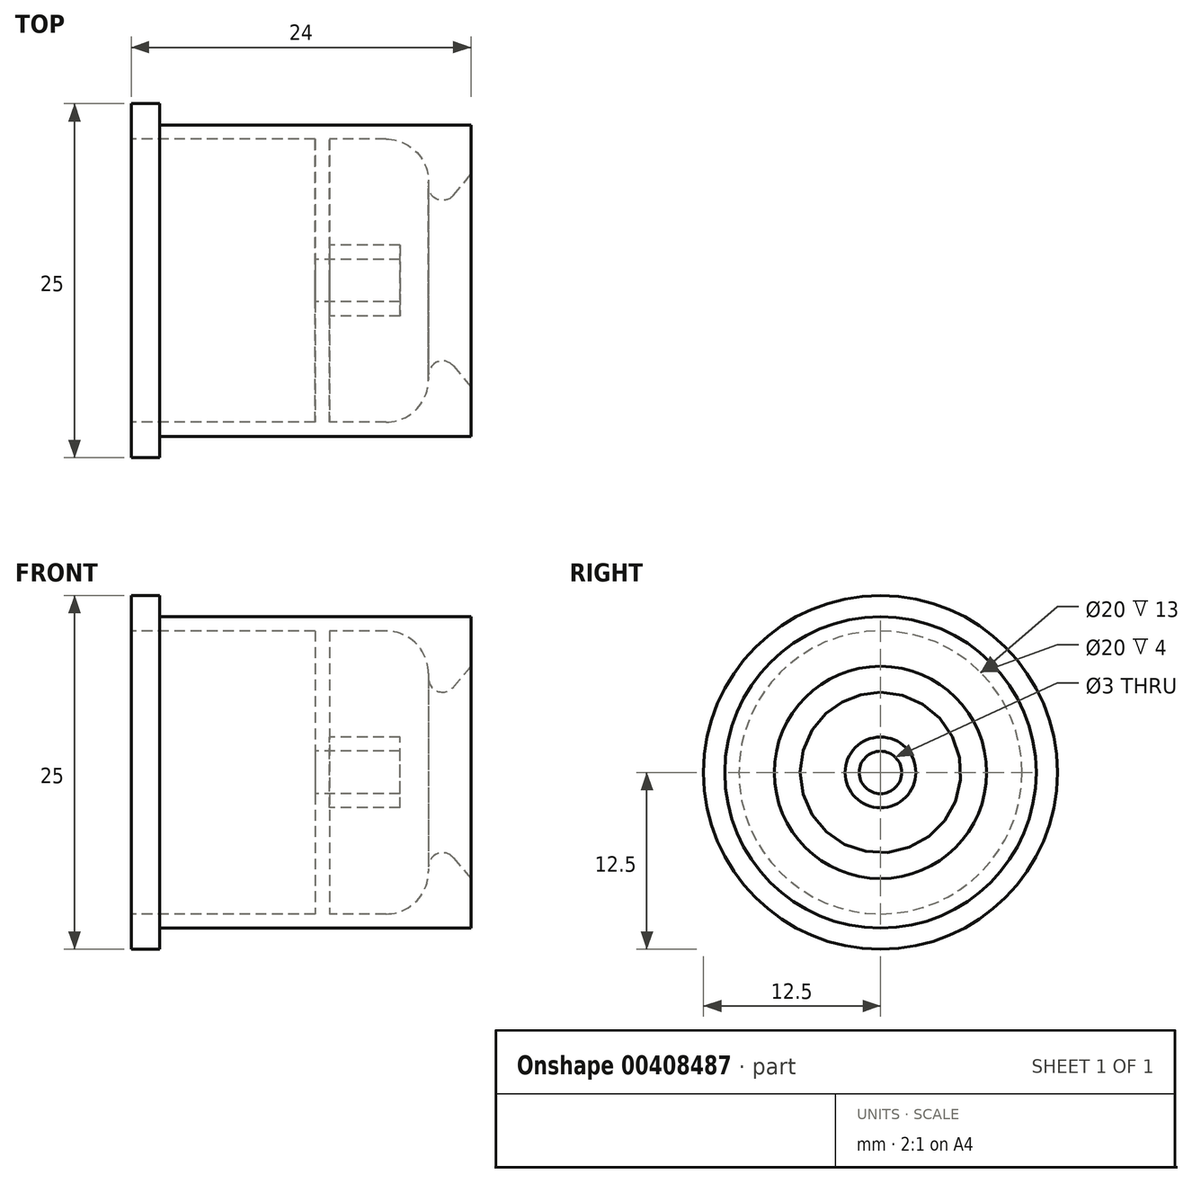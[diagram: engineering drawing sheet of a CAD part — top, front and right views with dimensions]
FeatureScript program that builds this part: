
annotation { "Feature Type Name" : "Feature", "Feature Type Description" : "" }
export const myFeature = defineFeature(function(context is Context, id is Id, definition is map)
    precondition{}
    {
        {
            var Q0;
            Q0=qCreatedBy(makeId("Front.planeOp"),FACE);
            var sketch = newSketch(context, id + "F0", { "sketchPlane" : qUnion([Q0])});
            skLineSegment(sketch, "E0", {"start": v(-26.94, 0) * mm, "end": v(26.94, 0) * mm, "construction": true});
            skLineSegment(sketch, "E1", {"start": v(-24, 10) * mm, "end": v(-6, 10) * mm});
            skLineSegment(sketch, "E2", {"start": v(-3, 7) * mm, "end": v(-3, 6.67) * mm});
            skLineSegment(sketch, "E3", {"start": v(-1.23, 6.03) * mm, "end": v(0, 7.5) * mm});
            skLineSegment(sketch, "E4", {"start": v(0, 7.5) * mm, "end": v(0, 11) * mm});
            skLineSegment(sketch, "E5", {"start": v(-22, 11) * mm, "end": v(-22, 12.5) * mm});
            skLineSegment(sketch, "E6", {"start": v(-22, 11) * mm, "end": v(0, 11) * mm});
            skLineSegment(sketch, "E7", {"start": v(-22, 12.5) * mm, "end": v(-24, 12.5) * mm});
            skLineSegment(sketch, "E8", {"start": v(-24, 12.5) * mm, "end": v(-24, 10) * mm});
            skPoint(sketch, "E9.visualSharp", {"position": v(-3, 10) * mm});
            skArc(sketch, "E9.filletArc", {"start": v(-3, 7) * mm, "mid": v(-3.88, 9.12) * mm, "end": v(-6, 10) * mm});
            skPoint(sketch, "E10.visualSharp", {"position": v(-3, 3.92) * mm});
            skArc(sketch, "E10.filletArc", {"start": v(-3, 6.67) * mm, "mid": v(-2.34, 5.73) * mm, "end": v(-1.23, 6.03) * mm});
            skSolve(sketch);
        }
        {
            var Q0;
            Q0=makeQuery(id+"F0.imprint","IMPRINT",FACE,{"disambiguationData":[TD([[makeQuery(id+"F0.imprint","IMPRINT",EDGE,{"derivedFrom":sQuery(id+"F0.wireOp",EDGE,"E1")}),1.0]])]});
            var Q1;
            Q1=sQuery(id+"F0.wireOp",EDGE,"E0");
            revolve(context, id + "F1", {"entities" : qUnion([Q0]), "axis" : qUnion([Q1]), "revolveType" : RevolveType.FULL});
        }
        {
            var Q0;
            Q0=makeQuery(id+"F1.opRevolve","SWEPT_FACE",FACE,{"disambiguationData":[OSD([sQuery(id+"F0.wireOp",EDGE,"E4")])]});
            cPlane(context, id + "F2", {"entities" : qUnion([Q0]), "cplaneType" : CPlaneType.OFFSET, "offset" : 11 * mm, "oppositeDirection" : true, "width" : 150 * mm, "height" : 150 * mm});
        }
        {
            var Q0;
            Q0=qCreatedBy(id+"F2.planeOp",FACE);
            var sketch = newSketch(context, id + "F3", { "sketchPlane" : qUnion([Q0])});
            skCircle(sketch, "E11", {"center": v(0, 0) * mm, "radius": 2.5 * mm});
            skSolve(sketch);
        }
        {
            var Q0;
            Q0=makeQuery(id+"F3.imprint","IMPRINT",FACE,{"disambiguationData":[TD([[makeQuery(id+"F3.imprint","IMPRINT",EDGE,{"derivedFrom":sQuery(id+"F3.wireOp",EDGE,"E11")}),1.0]])]});
            extrude(context, id + "F4", {"entities" : qUnion([Q0]), "depth" : 6 * mm});
        }
        {
            var Q0;
            Q0=makeQuery(id+"F4.opExtrude","CAP_FACE",FACE,{"disambiguationData":[OSD([sQuery(id+"F3.wireOp",EDGE,"E11")])],"isStart":true});
            var sketch = newSketch(context, id + "F5", { "sketchPlane" : qUnion([Q0])});
            skCircle(sketch, "E12.0", {"center": v(0, 0) * mm, "radius": 10 * mm});
            skLineSegment(sketch, "E13", {"start": v(0, 0) * mm, "end": v(0, 10) * mm, "construction": true});
            skLineSegment(sketch, "E14.0", {"start": v(0.75, 0) * mm, "end": v(0.75, 9.97) * mm});
            skLineSegment(sketch, "E15.0", {"start": v(-0.75, 0) * mm, "end": v(-0.75, 9.97) * mm});
            skLineSegment(sketch, "E16", {"start": v(-0.75, 0) * mm, "end": v(0.75, 0) * mm});
            skArc(sketch, "E17", {"start": v(-0.75, 9.97) * mm, "mid": v(0, 10) * mm, "end": v(0.75, 9.97) * mm});
            skSolve(sketch);
        }
        {
            var Q0;
            {var subQ0=sQuery(id+"F5.wireOp",EDGE,"E14.0");var subQ1=sQuery(id+"F5.wireOp",EDGE,"E12.0");var subQ2=makeQuery(id+"F5.imprint","INTERSECT",VERTEX,{"derivedFrom":[subQ1,subQ0]});Q0=makeQuery(id+"F5.imprint","IMPRINT",FACE,{"disambiguationData":[TD([[makeQuery(id+"F5.imprint","IMPRINT",EDGE,{"disambiguationData":[TD([[subQ2,-1.0]])],"derivedFrom":subQ1}),1.0]])]});}
            extrude(context, id + "F6", {"entities" : qUnion([Q0]), "operationType" : NewBodyOperationType.ADD, "oppositeDirection" : true, "depth" : 1 * mm});
        }
        {
            var Q0;
            Q0=makeQuery(id+"F1.opRevolve","SWEPT_BODY",BODY,{"disambiguationData":[OSD([sQuery(id+"F0.wireOp",EDGE,"E1"),sQuery(id+"F0.wireOp",EDGE,"E2"),sQuery(id+"F0.wireOp",EDGE,"E3"),sQuery(id+"F0.wireOp",EDGE,"E4"),sQuery(id+"F0.wireOp",EDGE,"E5"),sQuery(id+"F0.wireOp",EDGE,"E6"),sQuery(id+"F0.wireOp",EDGE,"E7"),sQuery(id+"F0.wireOp",EDGE,"E8"),sQuery(id+"F0.wireOp",EDGE,"E9.filletArc"),sQuery(id+"F0.wireOp",EDGE,"E10.filletArc")])]});
            var Q1;
            Q1=makeQuery(id+"F4.opExtrude","CAP_EDGE",EDGE,{"disambiguationData":[OSD([sQuery(id+"F3.wireOp",EDGE,"E11")])],"isStart":true});
            circularPattern(context, id + "F7", {"entities" : qUnion([Q0]), "axis" : qUnion([Q1]), "angle" : 360 * degree, "instanceCount" : 3, "equalSpace" : true});
        }
        {
            var Q0;
            Q0=makeQuery(id+"F1.opRevolve","SWEPT_BODY",BODY,{"disambiguationData":[OSD([sQuery(id+"F0.wireOp",EDGE,"E1"),sQuery(id+"F0.wireOp",EDGE,"E2"),sQuery(id+"F0.wireOp",EDGE,"E3"),sQuery(id+"F0.wireOp",EDGE,"E4"),sQuery(id+"F0.wireOp",EDGE,"E5"),sQuery(id+"F0.wireOp",EDGE,"E6"),sQuery(id+"F0.wireOp",EDGE,"E7"),sQuery(id+"F0.wireOp",EDGE,"E8"),sQuery(id+"F0.wireOp",EDGE,"E9.filletArc"),sQuery(id+"F0.wireOp",EDGE,"E10.filletArc")])]});
            var Q1;
            Q1=makeQuery(id+"F4.opExtrude","SWEPT_BODY",BODY,{"disambiguationData":[OSD([sQuery(id+"F3.wireOp",EDGE,"E11")])]});
            var Q2;
            Q2=makeQuery(id+"F7.opPattern","COPY",BODY,{"derivedFrom":makeQuery(id+"F1.opRevolve","SWEPT_BODY",BODY,{"disambiguationData":[OSD([sQuery(id+"F0.wireOp",EDGE,"E1"),sQuery(id+"F0.wireOp",EDGE,"E2"),sQuery(id+"F0.wireOp",EDGE,"E3"),sQuery(id+"F0.wireOp",EDGE,"E4"),sQuery(id+"F0.wireOp",EDGE,"E5"),sQuery(id+"F0.wireOp",EDGE,"E6"),sQuery(id+"F0.wireOp",EDGE,"E7"),sQuery(id+"F0.wireOp",EDGE,"E8"),sQuery(id+"F0.wireOp",EDGE,"E9.filletArc"),sQuery(id+"F0.wireOp",EDGE,"E10.filletArc")])]}),"instanceName":"2"});
            var Q3;
            Q3=makeQuery(id+"F7.opPattern","COPY",BODY,{"derivedFrom":makeQuery(id+"F1.opRevolve","SWEPT_BODY",BODY,{"disambiguationData":[OSD([sQuery(id+"F0.wireOp",EDGE,"E1"),sQuery(id+"F0.wireOp",EDGE,"E2"),sQuery(id+"F0.wireOp",EDGE,"E3"),sQuery(id+"F0.wireOp",EDGE,"E4"),sQuery(id+"F0.wireOp",EDGE,"E5"),sQuery(id+"F0.wireOp",EDGE,"E6"),sQuery(id+"F0.wireOp",EDGE,"E7"),sQuery(id+"F0.wireOp",EDGE,"E8"),sQuery(id+"F0.wireOp",EDGE,"E9.filletArc"),sQuery(id+"F0.wireOp",EDGE,"E10.filletArc")])]}),"instanceName":"1"});
            booleanBodies(context, id + "F8", {"operationType" : BooleanOperationType.UNION, "tools" : qUnion([Q0, Q1, Q2, Q3])});
        }
        {
            var Q0;
            {var subQ0=sQuery(id+"F3.wireOp",EDGE,"E11");var subQ1=makeQuery(id+"F6.opExtrude","CAP_FACE",FACE,{"disambiguationData":[OSD([subQ0,sQuery(id+"F5.wireOp",EDGE,"E12.0"),sQuery(id+"F5.wireOp",EDGE,"E14.0"),sQuery(id+"F5.wireOp",EDGE,"E15.0")])],"isStart":true});Q0=makeQuery(id+"F8.opBoolean","MERGE",FACE,{"derivedFrom":[makeQuery(id+"F4.opExtrude","CAP_FACE",FACE,{"disambiguationData":[OSD([subQ0])],"isStart":true}),subQ1,makeQuery(id+"F7.opPattern","COPY",FACE,{"derivedFrom":subQ1,"instanceName":"1"}),makeQuery(id+"F7.opPattern","COPY",FACE,{"derivedFrom":subQ1,"instanceName":"2"})]});}
            var sketch = newSketch(context, id + "F9", { "sketchPlane" : qUnion([Q0])});
            skCircle(sketch, "E18", {"center": v(0, 0) * mm, "radius": 1.5 * mm});
            skSolve(sketch);
        }
        {
            var Q0;
            Q0=makeQuery(id+"F9.imprint","IMPRINT",FACE,{"disambiguationData":[TD([[makeQuery(id+"F9.imprint","IMPRINT",EDGE,{"derivedFrom":sQuery(id+"F9.wireOp",EDGE,"E18")}),1.0]])]});
            extrude(context, id + "F10", {"entities" : qUnion([Q0]), "operationType" : NewBodyOperationType.REMOVE, "oppositeDirection" : true, "depth" : 25 * mm});
        }
    });
